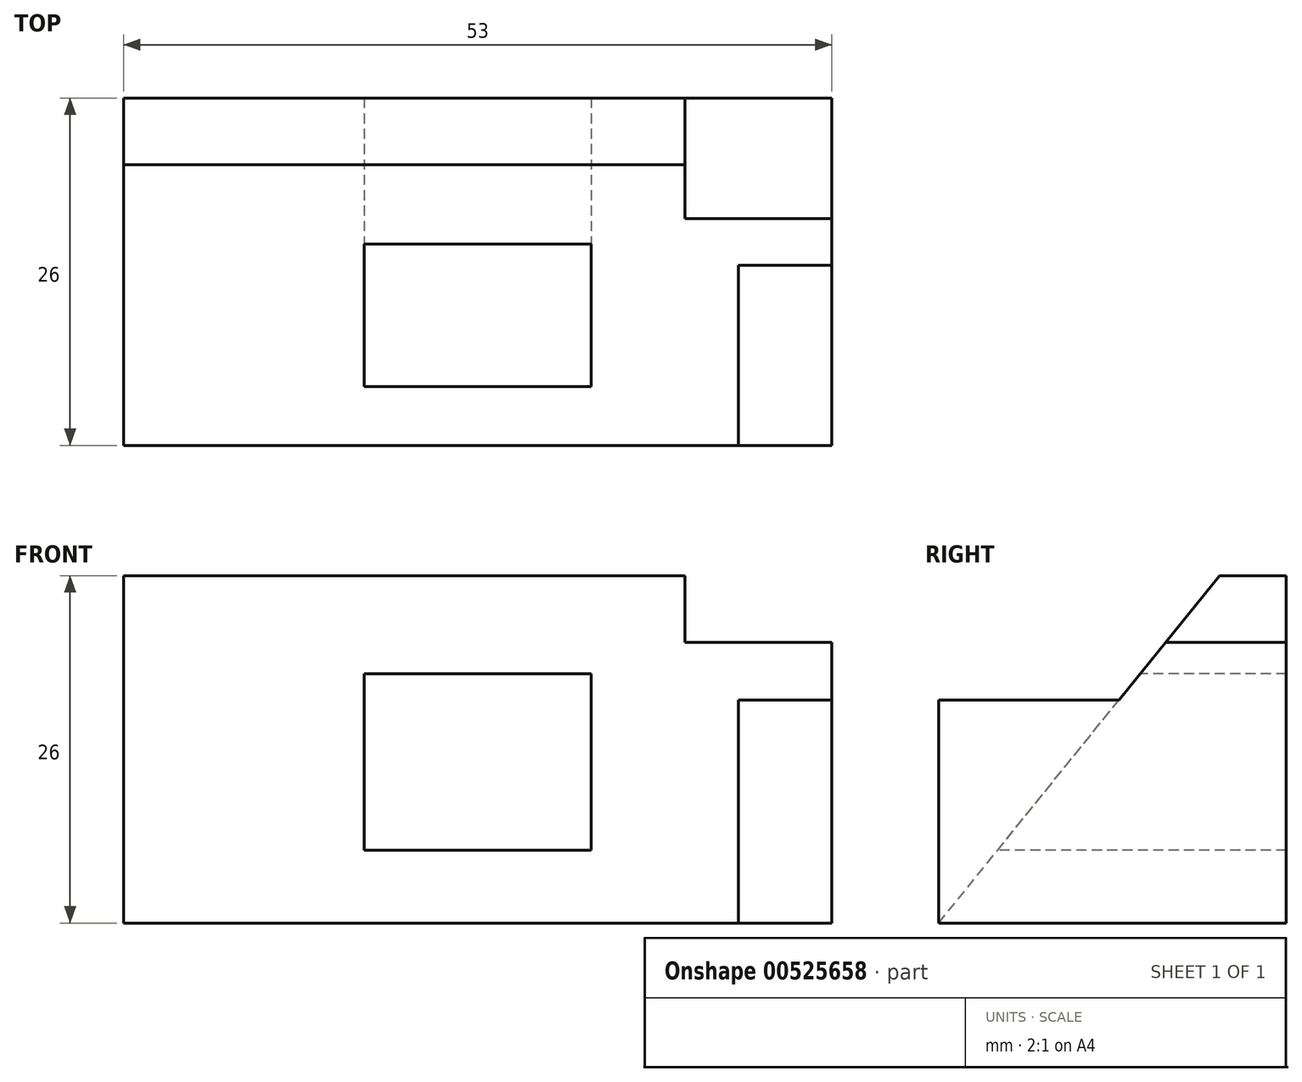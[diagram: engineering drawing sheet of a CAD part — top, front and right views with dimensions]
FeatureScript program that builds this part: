
annotation { "Feature Type Name" : "Feature", "Feature Type Description" : "" }
export const myFeature = defineFeature(function(context is Context, id is Id, definition is map)
    precondition{}
    {
        {
            var Q0;
            Q0=qCreatedBy(makeId("Top.planeOp"),FACE);
            var sketch = newSketch(context, id + "F0", { "sketchPlane" : qUnion([Q0])});
            skLineSegment(sketch, "E0.bottom", {"start": v(-26.5, 13) * mm, "end": v(26.5, 13) * mm});
            skLineSegment(sketch, "E0.top", {"start": v(-26.5, -13) * mm, "end": v(26.5, -13) * mm});
            skLineSegment(sketch, "E0.left", {"start": v(-26.5, 13) * mm, "end": v(-26.5, -13) * mm});
            skLineSegment(sketch, "E0.right", {"start": v(26.5, 13) * mm, "end": v(26.5, -13) * mm});
            skPoint(sketch, "E0.middle", {"position": v(0, 0) * mm});
            skSolve(sketch);
        }
        {
            var Q0;
            Q0=makeQuery(id+"F0.imprint","IMPRINT",FACE,{"disambiguationData":[TD([[makeQuery(id+"F0.imprint","IMPRINT",EDGE,{"derivedFrom":sQuery(id+"F0.wireOp",EDGE,"E0.bottom")}),-1.0]])]});
            extrude(context, id + "F1", {"entities" : qUnion([Q0]), "depth" : 26 * mm, "offsetDistance" : 25 * mm});
        }
        {
            var Q0;
            Q0=makeQuery(id+"F1.opExtrude","SWEPT_FACE",FACE,{"disambiguationData":[OSD([sQuery(id+"F0.wireOp",EDGE,"E0.right")])]});
            var sketch = newSketch(context, id + "F2", { "sketchPlane" : qUnion([Q0])});
            skLineSegment(sketch, "E1.0", {"start": v(13, 26) * mm, "end": v(-13, 26) * mm});
            skLineSegment(sketch, "E2.0", {"start": v(-13, 26) * mm, "end": v(-13, 0) * mm});
            skLineSegment(sketch, "E3", {"start": v(-13, 0) * mm, "end": v(8, 26) * mm});
            skLineSegment(sketch, "E4.0", {"start": v(13, 26) * mm, "end": v(13, 0) * mm});
            skLineSegment(sketch, "E5", {"start": v(3.96, 21) * mm, "end": v(13, 21) * mm});
            skLineSegment(sketch, "E6", {"start": v(0.49, 16.7) * mm, "end": v(-13, 16.7) * mm});
            skSolve(sketch);
        }
        {
            var Q0;
            {var subQ0=sQuery(id+"F2.wireOp",EDGE,"E2.0");Q0=makeQuery(id+"F2.imprint","IMPRINT",FACE,{"disambiguationData":[TD([[makeQuery(id+"F2.imprint","IMPRINT",EDGE,{"derivedFrom":subQ0}),1.0]])]});}
            var Q1;
            {var subQ2=sQuery(id+"F2.wireOp",EDGE,"E6");Q1=makeQuery(id+"F2.imprint","IMPRINT",FACE,{"disambiguationData":[TD([[makeQuery(id+"F2.imprint","IMPRINT",EDGE,{"derivedFrom":subQ2}),-1.0]])]});}
            extrude(context, id + "F3", {"entities" : qUnion([Q0, Q1]), "operationType" : NewBodyOperationType.REMOVE, "endBound" : BoundingType.THROUGH_ALL, "oppositeDirection" : true, "depth" : 25 * mm, "offsetDistance" : 25 * mm});
        }
        {
            var Q0;
            {var subQ3=sQuery(id+"F2.wireOp",EDGE,"E6");Q0=makeQuery(id+"F2.imprint","IMPRINT",FACE,{"disambiguationData":[TD([[makeQuery(id+"F2.imprint","IMPRINT",EDGE,{"derivedFrom":subQ3}),1.0]])]});}
            extrude(context, id + "F4", {"entities" : qUnion([Q0]), "operationType" : NewBodyOperationType.ADD, "oppositeDirection" : true, "depth" : 7 * mm, "offsetDistance" : 25 * mm});
        }
        {
            var Q0;
            {var subQ5=sQuery(id+"F2.wireOp",EDGE,"E5");Q0=makeQuery(id+"F2.imprint","IMPRINT",FACE,{"disambiguationData":[TD([[makeQuery(id+"F2.imprint","IMPRINT",EDGE,{"derivedFrom":subQ5}),1.0]])]});}
            extrude(context, id + "F5", {"entities" : qUnion([Q0]), "operationType" : NewBodyOperationType.REMOVE, "oppositeDirection" : true, "depth" : 11 * mm, "offsetDistance" : 25 * mm});
        }
        {
            var Q0;
            Q0=makeQuery(id+"F3.boolean.opBoolean","COPY",FACE,{"derivedFrom":makeQuery(id+"F3.opExtrude","SWEPT_FACE",FACE,{"disambiguationData":[OSD([sQuery(id+"F2.wireOp",EDGE,"E3")])]})});
            var sketch = newSketch(context, id + "F6", { "sketchPlane" : qUnion([Q0])});
            skLineSegment(sketch, "E7", {"start": v(-19.5, -1.17) * mm, "end": v(19.5, -1.17) * mm, "construction": true});
            skLineSegment(sketch, "E8.bottom", {"start": v(-8.5, 15.83) * mm, "end": v(8.5, 15.83) * mm});
            skLineSegment(sketch, "E8.top", {"start": v(-8.5, -1.17) * mm, "end": v(8.5, -1.17) * mm});
            skLineSegment(sketch, "E8.left", {"start": v(-8.5, 15.83) * mm, "end": v(-8.5, -1.17) * mm});
            skLineSegment(sketch, "E8.right", {"start": v(8.5, 15.83) * mm, "end": v(8.5, -1.17) * mm});
            skPoint(sketch, "E8.middle", {"position": v(0, 7.33) * mm});
            skSolve(sketch);
        }
        {
            var Q0;
            Q0=sQuery(id+"F6.wireOp",EDGE,"E8.right");
            cPlane(context, id + "F7", {"entities" : qUnion([Q0]), "cplaneType" : CPlaneType.LINE_ANGLE, "offset" : 25 * mm, "angle" : 0 * degree, "width" : 150 * mm, "height" : 150 * mm});
        }
        {
            var Q0;
            Q0=qCreatedBy(id+"F7.planeOp",FACE);
            var sketch = newSketch(context, id + "F8", { "sketchPlane" : qUnion([Q0])});
            skLineSegment(sketch, "E9", {"start": v(-2.08, 18.67) * mm, "end": v(30.92, 18.67) * mm});
            skLineSegment(sketch, "E10", {"start": v(8.6, 5.45) * mm, "end": v(30.92, 5.45) * mm});
            skLineSegment(sketch, "E11", {"start": v(30.92, 18.67) * mm, "end": v(30.92, 5.45) * mm});
            skSolve(sketch);
        }
        {
            var Q0;
            Q0=sQuery(id+"F6.wireOp",EDGE,"E8.left");
            cPlane(context, id + "F9", {"entities" : qUnion([Q0]), "cplaneType" : CPlaneType.LINE_ANGLE, "offset" : 25 * mm, "angle" : 0 * degree, "width" : 150 * mm, "height" : 150 * mm});
        }
        {
            var Q0;
            Q0=qCreatedBy(id+"F9.planeOp",FACE);
            var sketch = newSketch(context, id + "F10", { "sketchPlane" : qUnion([Q0])});
            skLineSegment(sketch, "E12", {"start": v(-2.08, 18.67) * mm, "end": v(30.92, 18.67) * mm});
            skLineSegment(sketch, "E13", {"start": v(8.6, 5.45) * mm, "end": v(30.92, 5.45) * mm});
            skLineSegment(sketch, "E14", {"start": v(30.92, 18.67) * mm, "end": v(30.92, 5.45) * mm});
            skSolve(sketch);
        }
        {
            var Q0;
            Q0=sQuery(id+"F8.wireOp",VERTEX,"E9.end");
            var Q1;
            Q1=sQuery(id+"F10.wireOp",VERTEX,"E12.end");
            var Q2;
            Q2=sQuery(id+"F10.wireOp",VERTEX,"E13.end");
            cPlane(context, id + "F11", {"entities" : qUnion([Q0, Q1, Q2]), "cplaneType" : CPlaneType.THREE_POINT, "offset" : 25 * mm, "width" : 150 * mm, "height" : 150 * mm});
        }
        {
            var Q0;
            Q0=qCreatedBy(id+"F11.planeOp",FACE);
            var sketch = newSketch(context, id + "F12", { "sketchPlane" : qUnion([Q0])});
            skLineSegment(sketch, "E15.0", {"start": v(8.5, 18.67) * mm, "end": v(-8.5, 18.67) * mm});
            skLineSegment(sketch, "E16.0", {"start": v(8.5, 18.67) * mm, "end": v(8.5, 5.45) * mm});
            skLineSegment(sketch, "E17.0", {"start": v(8.5, 5.45) * mm, "end": v(-8.5, 5.45) * mm});
            skLineSegment(sketch, "E18.0", {"start": v(-8.5, 18.67) * mm, "end": v(-8.5, 5.45) * mm});
            skSolve(sketch);
        }
        {
            var Q0;
            Q0=makeQuery(id+"F12.imprint","IMPRINT",FACE,{"disambiguationData":[TD([[makeQuery(id+"F12.imprint","IMPRINT",EDGE,{"derivedFrom":sQuery(id+"F12.wireOp",EDGE,"E15.0")}),1.0]])]});
            extrude(context, id + "F13", {"entities" : qUnion([Q0]), "operationType" : NewBodyOperationType.REMOVE, "endBound" : BoundingType.THROUGH_ALL, "depth" : 25 * mm, "offsetDistance" : 25 * mm});
        }
    });
